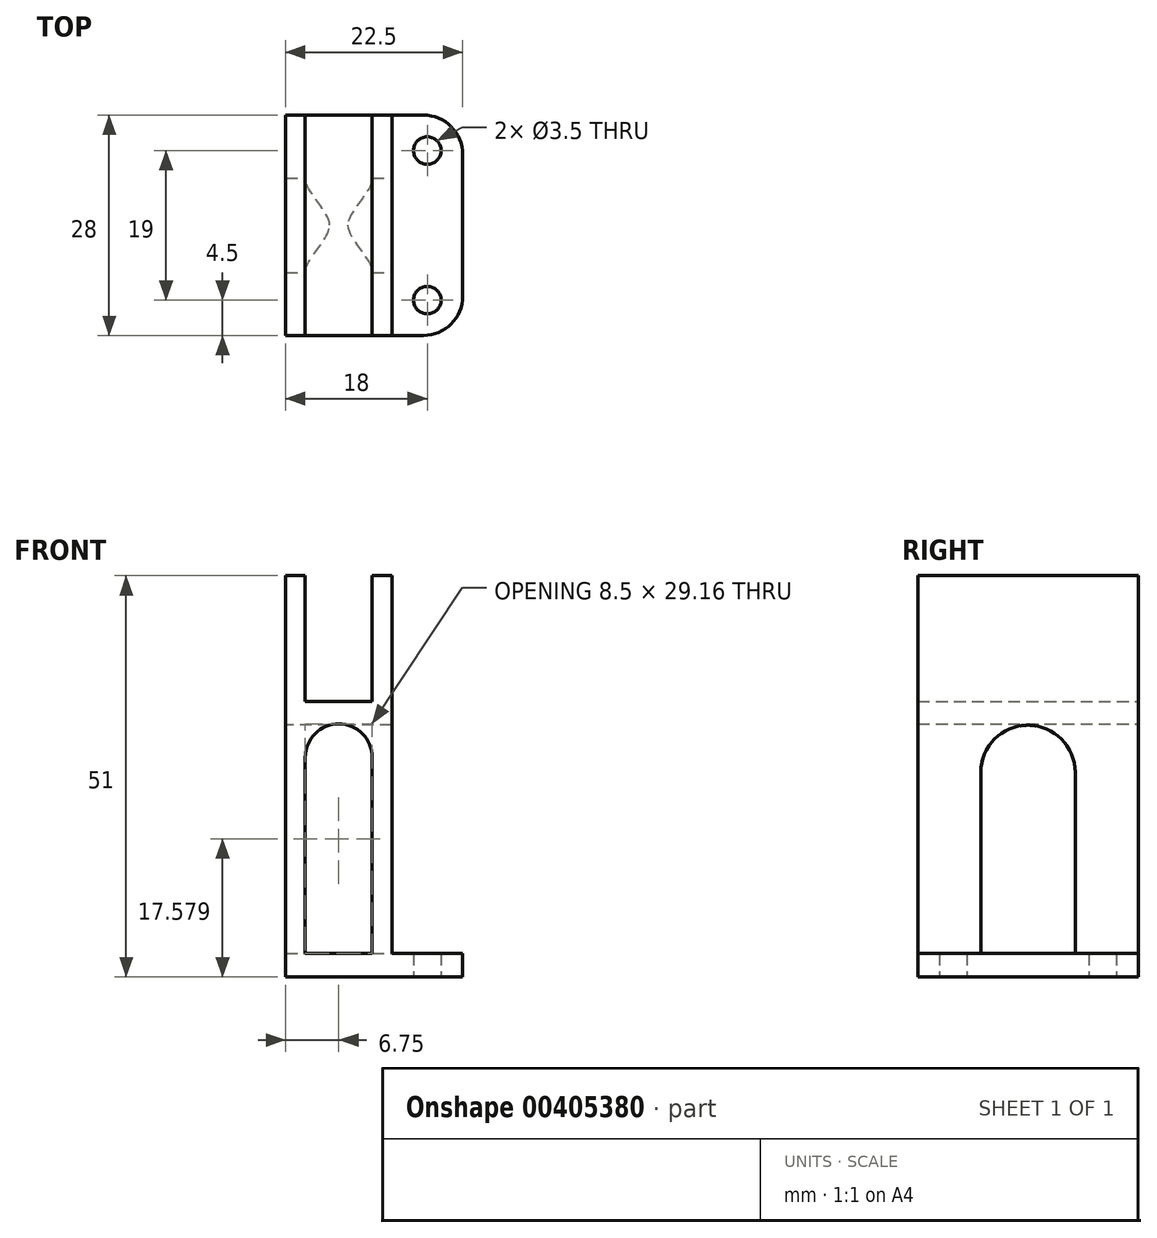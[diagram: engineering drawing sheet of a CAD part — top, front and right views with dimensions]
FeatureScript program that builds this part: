
annotation { "Feature Type Name" : "Feature", "Feature Type Description" : "" }
export const myFeature = defineFeature(function(context is Context, id is Id, definition is map)
    precondition{}
    {
        {
            var Q0;
            Q0=qCreatedBy(makeId("Front.planeOp"),FACE);
            var sketch = newSketch(context, id + "F0", { "sketchPlane" : qUnion([Q0])});
            skLineSegment(sketch, "E0.bottom", {"start": v(-6.75, 25.5) * mm, "end": v(-4.25, 25.5) * mm});
            skLineSegment(sketch, "E0.top", {"start": v(-6.75, -25.5) * mm, "end": v(-4.25, -25.5) * mm});
            skLineSegment(sketch, "E0.left", {"start": v(-6.75, 25.5) * mm, "end": v(-6.75, -25.5) * mm});
            skLineSegment(sketch, "E0.right", {"start": v(6.75, 25.5) * mm, "end": v(6.75, -22.5) * mm});
            skPoint(sketch, "E0.middle", {"position": v(0, 0) * mm});
            skLineSegment(sketch, "E1", {"start": v(-4.25, 25.5) * mm, "end": v(-4.25, 9.5) * mm});
            skLineSegment(sketch, "E2", {"start": v(-4.25, 9.5) * mm, "end": v(0, 9.5) * mm});
            skLineSegment(sketch, "E3.MirrorCS", {"start": v(4.25, 25.5) * mm, "end": v(4.25, 9.5) * mm});
            skLineSegment(sketch, "E4.MirrorCS", {"start": v(4.25, 9.5) * mm, "end": v(0, 9.5) * mm});
            skLineSegment(sketch, "E5.trimOffspring", {"start": v(4.25, 25.5) * mm, "end": v(6.75, 25.5) * mm});
            skLineSegment(sketch, "E6", {"start": v(-4.25, -22.5) * mm, "end": v(-4.25, 6.66) * mm});
            skLineSegment(sketch, "E7", {"start": v(-4.25, 6.66) * mm, "end": v(0, 6.66) * mm});
            skLineSegment(sketch, "E8.MirrorCS", {"start": v(4.25, 6.66) * mm, "end": v(0, 6.66) * mm});
            skLineSegment(sketch, "E9.MirrorCS", {"start": v(4.25, -22.5) * mm, "end": v(4.25, 6.66) * mm});
            skLineSegment(sketch, "E10.trimOffspring", {"start": v(4.25, -25.5) * mm, "end": v(6.75, -25.5) * mm});
            skLineSegment(sketch, "E11.bottom", {"start": v(-6.75, -25.5) * mm, "end": v(15.75, -25.5) * mm});
            skLineSegment(sketch, "E11.top", {"start": v(-4.25, -22.5) * mm, "end": v(4.25, -22.5) * mm});
            skLineSegment(sketch, "E11.left", {"start": v(-6.75, -25.5) * mm, "end": v(-6.75, -22.5) * mm});
            skLineSegment(sketch, "E11.right", {"start": v(15.75, -25.5) * mm, "end": v(15.75, -22.5) * mm});
            skLineSegment(sketch, "E12.trimOffspring", {"start": v(6.75, -22.5) * mm, "end": v(15.75, -22.5) * mm});
            skSolve(sketch);
        }
        {
            var Q0;
            Q0=makeQuery(id+"F0.imprint","IMPRINT",FACE,{"disambiguationData":[TD([[makeQuery(id+"F0.imprint","IMPRINT",EDGE,{"derivedFrom":sQuery(id+"F0.wireOp",EDGE,"E0.bottom")}),-1.0]])]});
            extrude(context, id + "F1", {"entities" : qUnion([Q0]), "depth" : 28 * mm});
        }
        {
            var Q0;
            Q0=makeQuery(id+"F1.opExtrude","SWEPT_FACE",FACE,{"disambiguationData":[OSD([sQuery(id+"F0.wireOp",EDGE,"E11.bottom")])]});
            var sketch = newSketch(context, id + "F2", { "sketchPlane" : qUnion([Q0])});
            skCircle(sketch, "E13", {"center": v(11.25, 23.5) * mm, "radius": 1.75 * mm});
            skCircle(sketch, "E14", {"center": v(11.25, 4.5) * mm, "radius": 1.75 * mm});
            skSolve(sketch);
        }
        {
            var Q0;
            Q0 = qSketchRegion(id + "F2", true);
            extrude(context, id + "F3", {"entities" : qUnion([Q0]), "operationType" : NewBodyOperationType.REMOVE, "oppositeDirection" : true, "depth" : 25 * mm});
        }
        {
            var Q0;
            Q0=makeQuery(id+"F1.opExtrude","SWEPT_FACE",FACE,{"disambiguationData":[OSD([sQuery(id+"F0.wireOp",EDGE,"E0.right")])]});
            var sketch = newSketch(context, id + "F4", { "sketchPlane" : qUnion([Q0])});
            skLineSegment(sketch, "E15.bottom", {"start": v(-20, -22.5) * mm, "end": v(-8, -22.5) * mm});
            skLineSegment(sketch, "E15.top", {"start": v(-20, 6.5) * mm, "end": v(-8, 6.5) * mm});
            skLineSegment(sketch, "E15.left", {"start": v(-20, -22.5) * mm, "end": v(-20, 6.5) * mm});
            skLineSegment(sketch, "E15.right", {"start": v(-8, -22.5) * mm, "end": v(-8, 6.5) * mm});
            skSolve(sketch);
        }
        {
            var Q0;
            Q0=makeQuery(id+"F4.imprint","IMPRINT",FACE,{"disambiguationData":[TD([[makeQuery(id+"F4.imprint","IMPRINT",EDGE,{"derivedFrom":sQuery(id+"F4.wireOp",EDGE,"E15.bottom")}),1.0]])]});
            extrude(context, id + "F5", {"entities" : qUnion([Q0]), "operationType" : NewBodyOperationType.REMOVE, "oppositeDirection" : true, "depth" : 25 * mm});
        }
        {
            var Q0;
            Q0=makeQuery(id+"F1.opExtrude","SWEPT_EDGE",EDGE,{"disambiguationData":[OSD([sQuery(id+"F0.wireOp",EDGE,"E8.MirrorCS"),sQuery(id+"F0.wireOp",EDGE,"E9.MirrorCS")])]});
            var Q1;
            Q1=makeQuery(id+"F1.opExtrude","SWEPT_EDGE",EDGE,{"disambiguationData":[OSD([sQuery(id+"F0.wireOp",EDGE,"E6"),sQuery(id+"F0.wireOp",EDGE,"E7")])]});
            fillet(context, id + "F6", {"entities" : qUnion([Q0, Q1]), "radius" : 4.25 * mm, "tangentPropagation" : true, "allowEdgeOverflow" : false});
        }
        {
            var Q0;
            {var subQ0=sQuery(id+"F4.wireOp",EDGE,"E15.left");var subQ1=sQuery(id+"F4.wireOp",EDGE,"E15.top");Q0=makeQuery(id+"F5.boolean.opBoolean","COPY",EDGE,{"disambiguationData":[TD([makeQuery(id+"F1.opExtrude","SWEPT_FACE",FACE,{"disambiguationData":[OSD([sQuery(id+"F0.wireOp",EDGE,"E0.right")])]})])],"derivedFrom":makeQuery(id+"F5.opExtrude","SWEPT_EDGE",EDGE,{"disambiguationData":[OSD([subQ1,subQ0])]})});}
            var Q1;
            {var subQ0=sQuery(id+"F4.wireOp",EDGE,"E15.top");var subQ1=sQuery(id+"F4.wireOp",EDGE,"E15.left");Q1=makeQuery(id+"F5.boolean.opBoolean","COPY",EDGE,{"disambiguationData":[TD([makeQuery(id+"F1.opExtrude","SWEPT_FACE",FACE,{"disambiguationData":[OSD([sQuery(id+"F0.wireOp",EDGE,"E6")])]})])],"derivedFrom":makeQuery(id+"F5.opExtrude","SWEPT_EDGE",EDGE,{"disambiguationData":[OSD([subQ0,subQ1])]})});}
            var Q2;
            {var subQ0=sQuery(id+"F4.wireOp",EDGE,"E15.top");var subQ1=sQuery(id+"F4.wireOp",EDGE,"E15.right");Q2=makeQuery(id+"F5.boolean.opBoolean","COPY",EDGE,{"disambiguationData":[TD([makeQuery(id+"F1.opExtrude","SWEPT_FACE",FACE,{"disambiguationData":[OSD([sQuery(id+"F0.wireOp",EDGE,"E6")])]})])],"derivedFrom":makeQuery(id+"F5.opExtrude","SWEPT_EDGE",EDGE,{"disambiguationData":[OSD([subQ0,subQ1])]})});}
            var Q3;
            {var subQ0=sQuery(id+"F4.wireOp",EDGE,"E15.top");var subQ1=sQuery(id+"F4.wireOp",EDGE,"E15.right");Q3=makeQuery(id+"F5.boolean.opBoolean","COPY",EDGE,{"disambiguationData":[TD([makeQuery(id+"F1.opExtrude","SWEPT_FACE",FACE,{"disambiguationData":[OSD([sQuery(id+"F0.wireOp",EDGE,"E0.right")])]})])],"derivedFrom":makeQuery(id+"F5.opExtrude","SWEPT_EDGE",EDGE,{"disambiguationData":[OSD([subQ0,subQ1])]})});}
            fillet(context, id + "F7", {"entities" : qUnion([Q0, Q1, Q2, Q3]), "radius" : 6 * mm, "tangentPropagation" : true, "allowEdgeOverflow" : false});
        }
        {
            var Q0;
            Q0=makeQuery(id+"F1.opExtrude","CAP_EDGE",EDGE,{"disambiguationData":[OSD([sQuery(id+"F0.wireOp",EDGE,"E11.right")])],"isStart":true});
            var Q1;
            Q1=makeQuery(id+"F1.opExtrude","CAP_EDGE",EDGE,{"disambiguationData":[OSD([sQuery(id+"F0.wireOp",EDGE,"E11.right")])],"isStart":false});
            fillet(context, id + "F8", {"entities" : qUnion([Q0, Q1]), "radius" : 5 * mm, "tangentPropagation" : true, "allowEdgeOverflow" : false});
        }
    });
